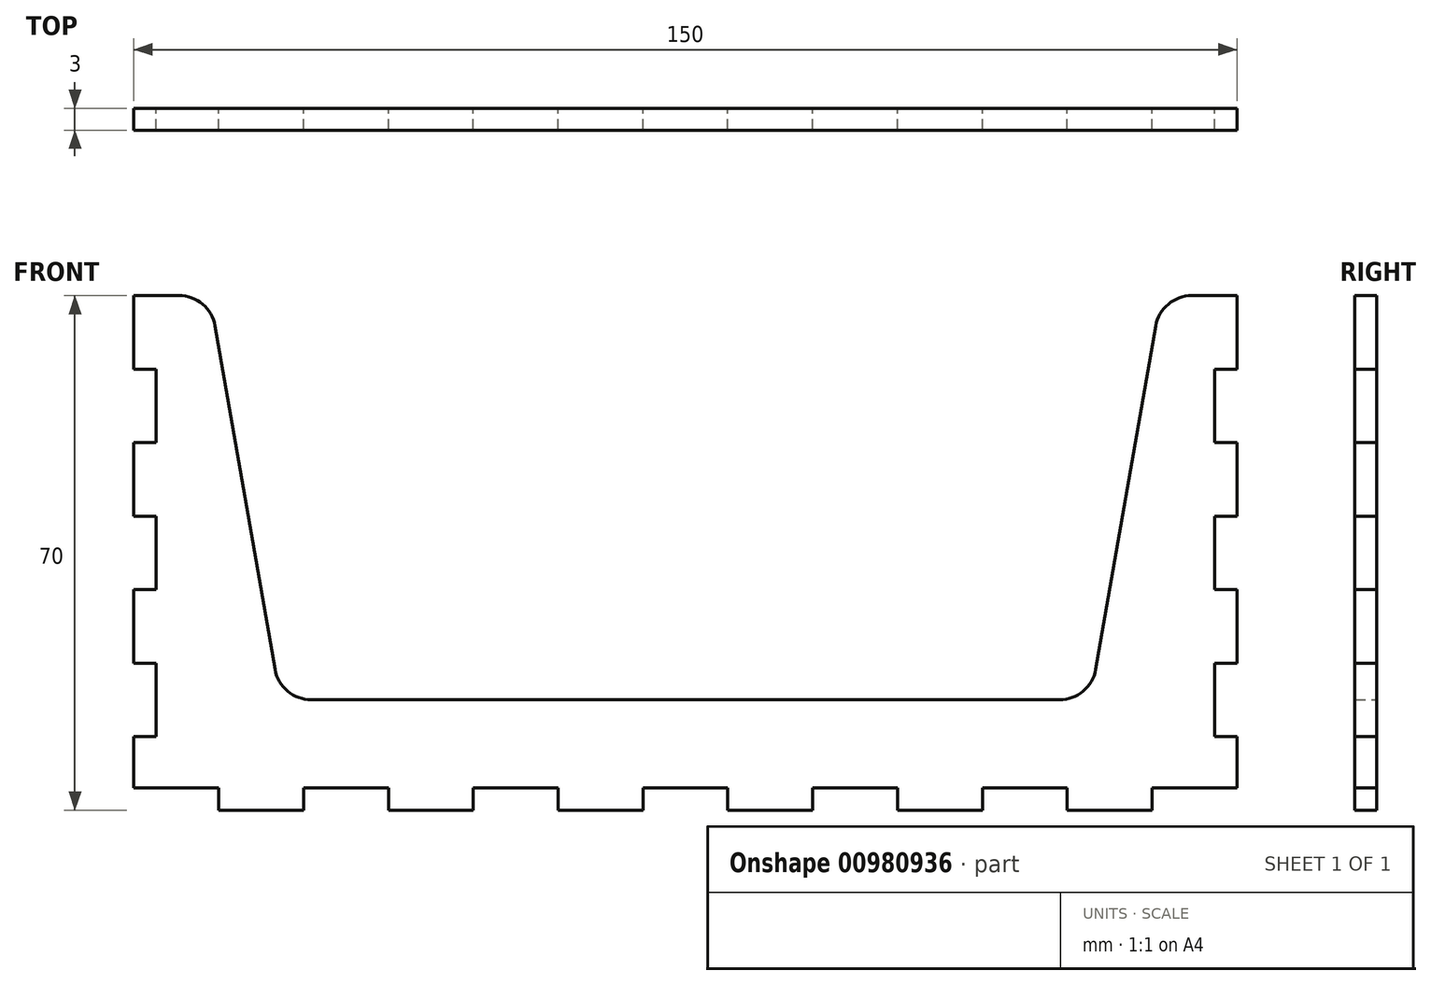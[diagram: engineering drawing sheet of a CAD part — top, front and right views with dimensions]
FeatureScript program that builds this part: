
annotation { "Feature Type Name" : "Feature", "Feature Type Description" : "" }
export const myFeature = defineFeature(function(context is Context, id is Id, definition is map)
    precondition{}
    {
        {
            var Q0;
            Q0=qCreatedBy(makeId("Front.planeOp"),FACE);
            var sketch = newSketch(context, id + "F0", { "sketchPlane" : qUnion([Q0])});
            skLineSegment(sketch, "E0.top", {"start": v(75, 35) * mm, "end": v(68.88, 35) * mm});
            skPoint(sketch, "E0.middle", {"position": v(0, 0) * mm});
            skLineSegment(sketch, "E1", {"start": v(-75, -32) * mm, "end": v(-63.46, -32) * mm});
            skLineSegment(sketch, "E2", {"start": v(-63.46, -32) * mm, "end": v(-63.46, -35) * mm});
            skLineSegment(sketch, "E3", {"start": v(-63.46, -35) * mm, "end": v(-51.92, -35) * mm});
            skLineSegment(sketch, "E4", {"start": v(-51.92, -35) * mm, "end": v(-51.92, -32) * mm});
            skLineSegment(sketch, "E5", {"start": v(-51.92, -32) * mm, "end": v(-40.38, -32) * mm});
            skLineSegment(sketch, "E6.1.0.0", {"start": v(-28.85, -32) * mm, "end": v(-17.3, -32) * mm});
            skLineSegment(sketch, "E6.1.0.2", {"start": v(-40.38, -35) * mm, "end": v(-28.85, -35) * mm});
            skLineSegment(sketch, "E6.1.0.3", {"start": v(-40.38, -32) * mm, "end": v(-40.38, -35) * mm});
            skLineSegment(sketch, "E6.1.0.4", {"start": v(-28.85, -35) * mm, "end": v(-28.85, -32) * mm});
            skLineSegment(sketch, "E6.2.0.0", {"start": v(-5.77, -32) * mm, "end": v(5.77, -32) * mm});
            skLineSegment(sketch, "E6.2.0.1", {"start": v(-28.85, -32) * mm, "end": v(-17.3, -32) * mm});
            skLineSegment(sketch, "E6.2.0.2", {"start": v(-17.3, -35) * mm, "end": v(-5.77, -35) * mm});
            skLineSegment(sketch, "E6.2.0.3", {"start": v(-17.3, -32) * mm, "end": v(-17.3, -35) * mm});
            skLineSegment(sketch, "E6.2.0.4", {"start": v(-5.77, -35) * mm, "end": v(-5.77, -32) * mm});
            skLineSegment(sketch, "E6.3.0.0", {"start": v(17.3, -32) * mm, "end": v(28.85, -32) * mm});
            skLineSegment(sketch, "E6.3.0.1", {"start": v(-5.77, -32) * mm, "end": v(5.77, -32) * mm});
            skLineSegment(sketch, "E6.3.0.2", {"start": v(5.77, -35) * mm, "end": v(17.3, -35) * mm});
            skLineSegment(sketch, "E6.3.0.3", {"start": v(5.77, -32) * mm, "end": v(5.77, -35) * mm});
            skLineSegment(sketch, "E6.3.0.4", {"start": v(17.3, -35) * mm, "end": v(17.3, -32) * mm});
            skLineSegment(sketch, "E6.4.0.0", {"start": v(40.38, -32) * mm, "end": v(51.92, -32) * mm});
            skLineSegment(sketch, "E6.4.0.1", {"start": v(17.3, -32) * mm, "end": v(28.85, -32) * mm});
            skLineSegment(sketch, "E6.4.0.2", {"start": v(28.85, -35) * mm, "end": v(40.38, -35) * mm});
            skLineSegment(sketch, "E6.4.0.3", {"start": v(28.85, -32) * mm, "end": v(28.85, -35) * mm});
            skLineSegment(sketch, "E6.4.0.4", {"start": v(40.38, -35) * mm, "end": v(40.38, -32) * mm});
            skLineSegment(sketch, "E6.5.0.0", {"start": v(63.46, -32) * mm, "end": v(75, -32) * mm});
            skLineSegment(sketch, "E6.5.0.1", {"start": v(40.38, -32) * mm, "end": v(51.92, -32) * mm});
            skLineSegment(sketch, "E6.5.0.2", {"start": v(51.92, -35) * mm, "end": v(63.46, -35) * mm});
            skLineSegment(sketch, "E6.5.0.3", {"start": v(51.92, -32) * mm, "end": v(51.92, -35) * mm});
            skLineSegment(sketch, "E6.5.0.4", {"start": v(63.46, -35) * mm, "end": v(63.46, -32) * mm});
            skLineSegment(sketch, "E6.direction1", {"start": v(-75, -32) * mm, "end": v(-63.46, -32) * mm, "construction": true});
            skLineSegment(sketch, "E7", {"start": v(-75, -32) * mm, "end": v(-75, -25) * mm});
            skLineSegment(sketch, "E8", {"start": v(-72, -25) * mm, "end": v(-72, -15) * mm});
            skLineSegment(sketch, "E9", {"start": v(-72, -15) * mm, "end": v(-75, -15) * mm});
            skLineSegment(sketch, "E10", {"start": v(-75, -25) * mm, "end": v(-72, -25) * mm});
            skLineSegment(sketch, "E11.1.0.1", {"start": v(-72, 5) * mm, "end": v(-75, 5) * mm});
            skLineSegment(sketch, "E11.1.0.3", {"start": v(-75, -5) * mm, "end": v(-72, -5) * mm});
            skLineSegment(sketch, "E11.2.0.1", {"start": v(-72, 25) * mm, "end": v(-75, 25) * mm});
            skLineSegment(sketch, "E11.2.0.3", {"start": v(-75, 15) * mm, "end": v(-72, 15) * mm});
            skLineSegment(sketch, "E11.2.0.5", {"start": v(-72, 15) * mm, "end": v(-72, 25) * mm});
            skLineSegment(sketch, "E12", {"start": v(-75, 5) * mm, "end": v(-75, 15) * mm});
            skPoint(sketch, "E13.orphan", {"position": v(-75, -5) * mm});
            skLineSegment(sketch, "E14", {"start": v(-75, -15) * mm, "end": v(-75, -5) * mm});
            skLineSegment(sketch, "E15", {"start": v(-72, -5) * mm, "end": v(-72, 5) * mm});
            skLineSegment(sketch, "E16", {"start": v(-75, 25) * mm, "end": v(-75, 35) * mm});
            skLineSegment(sketch, "E17.MirrorCS", {"start": v(75, -5) * mm, "end": v(72, -5) * mm});
            skLineSegment(sketch, "E18.MirrorCS", {"start": v(72, -15) * mm, "end": v(75, -15) * mm});
            skLineSegment(sketch, "E19.MirrorCS", {"start": v(75, 15) * mm, "end": v(72, 15) * mm});
            skLineSegment(sketch, "E20.MirrorCS", {"start": v(75, -25) * mm, "end": v(72, -25) * mm});
            skLineSegment(sketch, "E21.MirrorCS", {"start": v(72, 5) * mm, "end": v(75, 5) * mm});
            skLineSegment(sketch, "E22.MirrorCS", {"start": v(72, 25) * mm, "end": v(75, 25) * mm});
            skPoint(sketch, "E23.MirrorP", {"position": v(75, -5) * mm});
            skLineSegment(sketch, "E24.MirrorCS", {"start": v(75, -32) * mm, "end": v(75, -25) * mm});
            skLineSegment(sketch, "E25.MirrorCS", {"start": v(75, 25) * mm, "end": v(75, 35) * mm});
            skLineSegment(sketch, "E26.MirrorCS", {"start": v(72, 15) * mm, "end": v(72, 25) * mm});
            skLineSegment(sketch, "E27.MirrorCS", {"start": v(72, -25) * mm, "end": v(72, -15) * mm});
            skLineSegment(sketch, "E28.MirrorCS", {"start": v(75, 5) * mm, "end": v(75, 15) * mm});
            skLineSegment(sketch, "E29.MirrorCS", {"start": v(72, -5) * mm, "end": v(72, 5) * mm});
            skLineSegment(sketch, "E30.MirrorCS", {"start": v(75, -15) * mm, "end": v(75, -5) * mm});
            skPoint(sketch, "E0.left.start.orphan", {"position": v(75, -35) * mm});
            skPoint(sketch, "E0.right.start.orphan", {"position": v(-75, -35) * mm});
            skLineSegment(sketch, "E31", {"start": v(-63.95, 30.86) * mm, "end": v(-55.8, -15.86) * mm});
            skLineSegment(sketch, "E32", {"start": v(-50.88, -20) * mm, "end": v(0, -20) * mm});
            skPoint(sketch, "E33.visualSharp", {"position": v(-55.08, -20) * mm});
            skArc(sketch, "E33.filletArc", {"start": v(-55.8, -15.86) * mm, "mid": v(-54.1, -18.83) * mm, "end": v(-50.88, -20) * mm});
            skArc(sketch, "E34.MirrorCS", {"start": v(55.8, -15.86) * mm, "mid": v(54.1, -18.83) * mm, "end": v(50.88, -20) * mm});
            skLineSegment(sketch, "E35.MirrorCS", {"start": v(63.95, 30.86) * mm, "end": v(55.8, -15.86) * mm});
            skPoint(sketch, "E36.MirrorP", {"position": v(55.08, -20) * mm});
            skLineSegment(sketch, "E37.MirrorCS", {"start": v(50.88, -20) * mm, "end": v(0, -20) * mm});
            skLineSegment(sketch, "E38.trimOffspring", {"start": v(-68.88, 35) * mm, "end": v(-75, 35) * mm});
            skPoint(sketch, "E39.visualSharp", {"position": v(-64.67, 35) * mm});
            skArc(sketch, "E39.filletArc", {"start": v(-63.95, 30.86) * mm, "mid": v(-65.66, 33.83) * mm, "end": v(-68.88, 35) * mm});
            skPoint(sketch, "E40.visualSharp", {"position": v(64.67, 35) * mm});
            skArc(sketch, "E40.filletArc", {"start": v(68.88, 35) * mm, "mid": v(65.66, 33.83) * mm, "end": v(63.95, 30.86) * mm});
            skSolve(sketch);
        }
        {
            var Q0;
            Q0=makeQuery(id+"F0.imprint","IMPRINT",FACE,{"disambiguationData":[TD([[makeQuery(id+"F0.imprint","IMPRINT",EDGE,{"derivedFrom":sQuery(id+"F0.wireOp",EDGE,"E0.top")}),1.0]])]});
            extrude(context, id + "F1", {"entities" : qUnion([Q0]), "depth" : 3 * mm, "offsetDistance" : 25 * mm});
        }
    });
